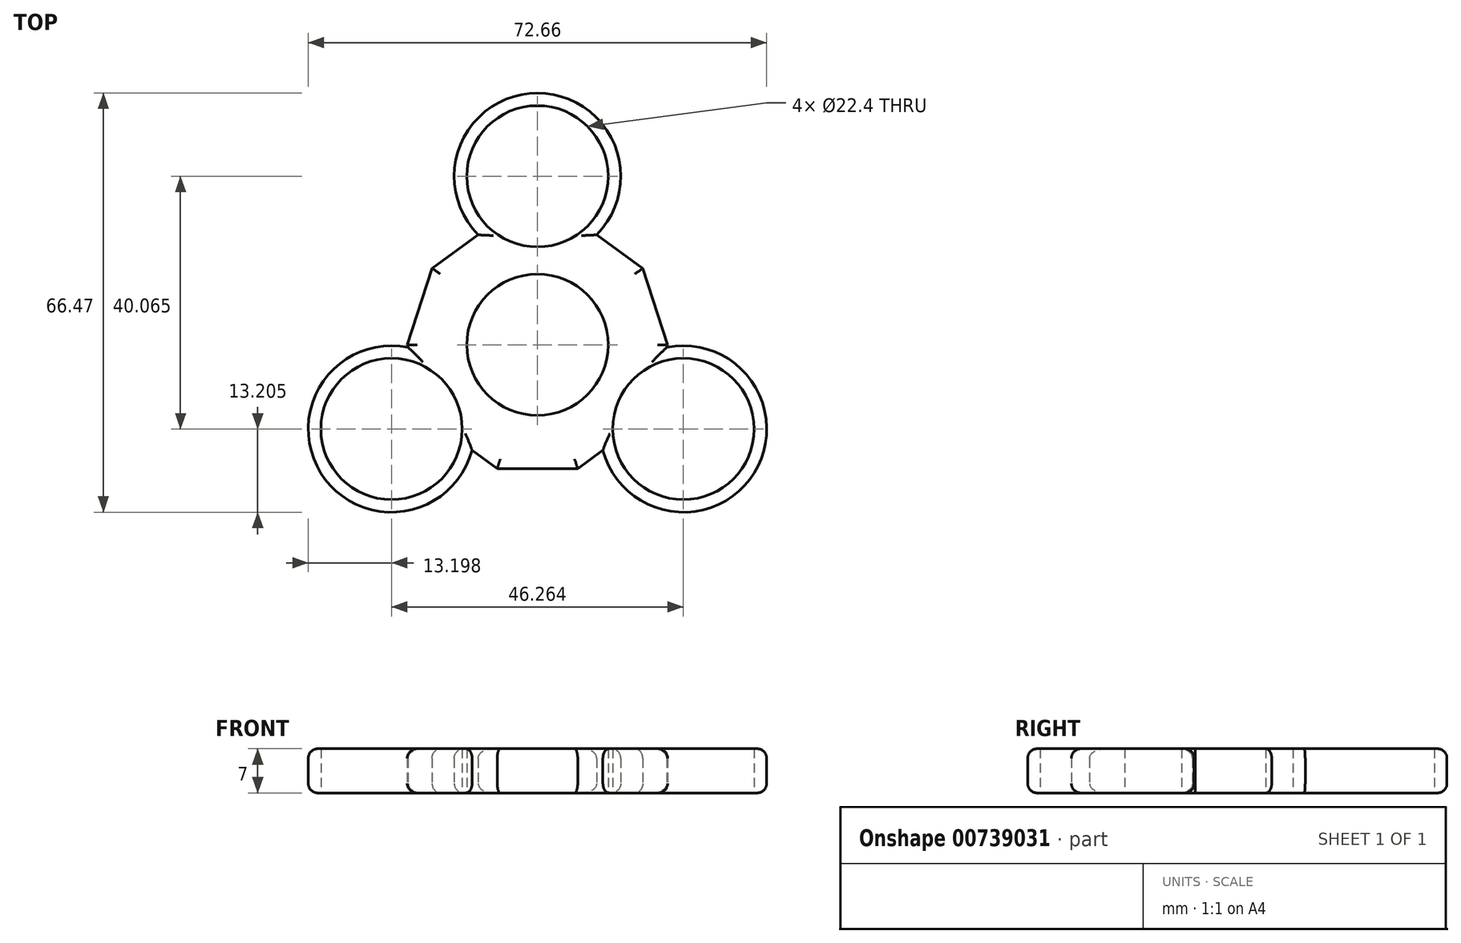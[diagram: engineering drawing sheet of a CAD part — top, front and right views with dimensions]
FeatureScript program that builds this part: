
annotation { "Feature Type Name" : "Feature", "Feature Type Description" : "" }
export const myFeature = defineFeature(function(context is Context, id is Id, definition is map)
    precondition{}
    {
        {
            var Q0;
            Q0=qCreatedBy(makeId("Top.planeOp"),FACE);
            var sketch = newSketch(context, id + "F0", { "sketchPlane" : qUnion([Q0])});
            skCircle(sketch, "E0", {"center": v(0, 0) * mm, "radius": 11.2 * mm});
            skCircle(sketch, "E1", {"center": v(0, 26.71) * mm, "radius": 11.2 * mm});
            skArc(sketch, "E2", {"start": v(9.4, 17.44) * mm, "mid": v(0, 39.91) * mm, "end": v(-9.4, 17.44) * mm});
            skArc(sketch, "E3.1.0", {"start": v(-20.5, -0.42) * mm, "mid": v(-34.34, -20.32) * mm, "end": v(-10.37, -16.73) * mm});
            skCircle(sketch, "E3.1.1", {"center": v(-23.13, -13.36) * mm, "radius": 11.2 * mm});
            skArc(sketch, "E3.2.0", {"start": v(10.37, -16.73) * mm, "mid": v(34.34, -20.32) * mm, "end": v(20.5, -0.42) * mm});
            skCircle(sketch, "E3.2.1", {"center": v(23.13, -13.36) * mm, "radius": 11.2 * mm});
            skLineSegment(sketch, "E4.0", {"start": v(6.38, -19.63) * mm, "end": v(-6.38, -19.63) * mm});
            skLineSegment(sketch, "E4.1", {"start": v(-6.38, -19.63) * mm, "end": v(-10.37, -16.73) * mm});
            skLineSegment(sketch, "E4.2", {"start": v(-20.5, -0.42) * mm, "end": v(-20.64, 0) * mm});
            skLineSegment(sketch, "E4.3", {"start": v(-20.64, 0) * mm, "end": v(-16.7, 12.13) * mm});
            skLineSegment(sketch, "E4.4", {"start": v(-16.7, 12.13) * mm, "end": v(-9.4, 17.44) * mm});
            skLineSegment(sketch, "E4.6", {"start": v(9.4, 17.44) * mm, "end": v(16.7, 12.13) * mm});
            skLineSegment(sketch, "E4.7", {"start": v(16.7, 12.13) * mm, "end": v(20.64, 0) * mm});
            skLineSegment(sketch, "E4.8", {"start": v(20.64, 0) * mm, "end": v(20.5, -0.42) * mm});
            skPoint(sketch, "E4.0.midPoint", {"position": v(0, -19.63) * mm});
            skPoint(sketch, "E5.orphan", {"position": v(-16.7, -12.13) * mm});
            skPoint(sketch, "E6.orphan", {"position": v(16.7, -12.13) * mm});
            skPoint(sketch, "E7.orphan", {"position": v(6.38, 19.63) * mm});
            skLineSegment(sketch, "E8.trimOffspring", {"start": v(10.37, -16.73) * mm, "end": v(6.38, -19.63) * mm});
            skSolve(sketch);
        }
        {
            var Q0;
            Q0=makeQuery(id+"F0.imprint","IMPRINT",FACE,{"disambiguationData":[TD([[makeQuery(id+"F0.imprint","IMPRINT",EDGE,{"derivedFrom":sQuery(id+"F0.wireOp",EDGE,"E0")}),-1.0]])]});
            extrude(context, id + "F1", {"entities" : qUnion([Q0]), "depth" : 7 * mm, "offsetDistance" : 25 * mm});
        }
        {
            var Q0;
            Q0=makeQuery(id+"F1.opExtrude","CAP_EDGE",EDGE,{"disambiguationData":[OSD([sQuery(id+"F0.wireOp",EDGE,"E4.0")])],"isStart":false});
            var Q1;
            Q1=makeQuery(id+"F1.opExtrude","CAP_EDGE",EDGE,{"disambiguationData":[OSD([sQuery(id+"F0.wireOp",EDGE,"E8.trimOffspring")])],"isStart":false});
            var Q2;
            Q2=makeQuery(id+"F1.opExtrude","CAP_EDGE",EDGE,{"disambiguationData":[OSD([sQuery(id+"F0.wireOp",EDGE,"E4.1")])],"isStart":false});
            var Q3;
            Q3=makeQuery(id+"F1.opExtrude","CAP_EDGE",EDGE,{"disambiguationData":[OSD([sQuery(id+"F0.wireOp",EDGE,"E4.3")])],"isStart":false});
            var Q4;
            Q4=makeQuery(id+"F1.opExtrude","CAP_EDGE",EDGE,{"disambiguationData":[OSD([sQuery(id+"F0.wireOp",EDGE,"E4.4")])],"isStart":false});
            var Q5;
            Q5=makeQuery(id+"F1.opExtrude","CAP_EDGE",EDGE,{"disambiguationData":[OSD([sQuery(id+"F0.wireOp",EDGE,"E4.7")])],"isStart":false});
            var Q6;
            Q6=makeQuery(id+"F1.opExtrude","CAP_EDGE",EDGE,{"disambiguationData":[OSD([sQuery(id+"F0.wireOp",EDGE,"E4.6")])],"isStart":false});
            var Q7;
            Q7=makeQuery(id+"F1.opExtrude","CAP_EDGE",EDGE,{"disambiguationData":[OSD([sQuery(id+"F0.wireOp",EDGE,"E2")])],"isStart":false});
            var Q8;
            Q8=makeQuery(id+"F1.opExtrude","CAP_EDGE",EDGE,{"disambiguationData":[OSD([sQuery(id+"F0.wireOp",EDGE,"E3.1.0")])],"isStart":false});
            var Q9;
            Q9=makeQuery(id+"F1.opExtrude","CAP_EDGE",EDGE,{"disambiguationData":[OSD([sQuery(id+"F0.wireOp",EDGE,"E3.2.0")])],"isStart":false});
            var Q10;
            Q10=makeQuery(id+"F1.opExtrude","CAP_EDGE",EDGE,{"disambiguationData":[OSD([sQuery(id+"F0.wireOp",EDGE,"E4.8")])],"isStart":false});
            var Q11;
            Q11=makeQuery(id+"F1.opExtrude","CAP_EDGE",EDGE,{"disambiguationData":[OSD([sQuery(id+"F0.wireOp",EDGE,"E4.2")])],"isStart":false});
            fillet(context, id + "F2", {"entities" : qUnion([Q0, Q1, Q2, Q3, Q4, Q5, Q6, Q7, Q8, Q9, Q10, Q11]), "radius" : 1.5 * mm, "tangentPropagation" : true, "allowEdgeOverflow" : false});
        }
        {
            var Q0;
            Q0=makeQuery(id+"F1.opExtrude","CAP_EDGE",EDGE,{"disambiguationData":[OSD([sQuery(id+"F0.wireOp",EDGE,"E4.6")])],"isStart":true});
            var Q1;
            Q1=makeQuery(id+"F1.opExtrude","CAP_EDGE",EDGE,{"disambiguationData":[OSD([sQuery(id+"F0.wireOp",EDGE,"E4.7")])],"isStart":true});
            var Q2;
            Q2=makeQuery(id+"F1.opExtrude","CAP_EDGE",EDGE,{"disambiguationData":[OSD([sQuery(id+"F0.wireOp",EDGE,"E3.2.0")])],"isStart":true});
            var Q3;
            Q3=makeQuery(id+"F1.opExtrude","CAP_EDGE",EDGE,{"disambiguationData":[OSD([sQuery(id+"F0.wireOp",EDGE,"E4.8")])],"isStart":true});
            var Q4;
            Q4=makeQuery(id+"F1.opExtrude","CAP_EDGE",EDGE,{"disambiguationData":[OSD([sQuery(id+"F0.wireOp",EDGE,"E4.4")])],"isStart":true});
            var Q5;
            Q5=makeQuery(id+"F1.opExtrude","CAP_EDGE",EDGE,{"disambiguationData":[OSD([sQuery(id+"F0.wireOp",EDGE,"E3.1.0")])],"isStart":true});
            var Q6;
            Q6=makeQuery(id+"F1.opExtrude","CAP_EDGE",EDGE,{"disambiguationData":[OSD([sQuery(id+"F0.wireOp",EDGE,"E4.2")])],"isStart":true});
            var Q7;
            Q7=makeQuery(id+"F1.opExtrude","CAP_EDGE",EDGE,{"disambiguationData":[OSD([sQuery(id+"F0.wireOp",EDGE,"E4.3")])],"isStart":true});
            var Q8;
            Q8=makeQuery(id+"F1.opExtrude","CAP_EDGE",EDGE,{"disambiguationData":[OSD([sQuery(id+"F0.wireOp",EDGE,"E4.0")])],"isStart":true});
            var Q9;
            Q9=makeQuery(id+"F1.opExtrude","CAP_EDGE",EDGE,{"disambiguationData":[OSD([sQuery(id+"F0.wireOp",EDGE,"E4.1")])],"isStart":true});
            var Q10;
            Q10=makeQuery(id+"F1.opExtrude","CAP_EDGE",EDGE,{"disambiguationData":[OSD([sQuery(id+"F0.wireOp",EDGE,"E8.trimOffspring")])],"isStart":true});
            var Q11;
            Q11=makeQuery(id+"F1.opExtrude","CAP_EDGE",EDGE,{"disambiguationData":[OSD([sQuery(id+"F0.wireOp",EDGE,"E2")])],"isStart":true});
            fillet(context, id + "F3", {"entities" : qUnion([Q0, Q1, Q2, Q3, Q4, Q5, Q6, Q7, Q8, Q9, Q10, Q11]), "radius" : 1.5 * mm, "tangentPropagation" : true, "allowEdgeOverflow" : false});
        }
    });
